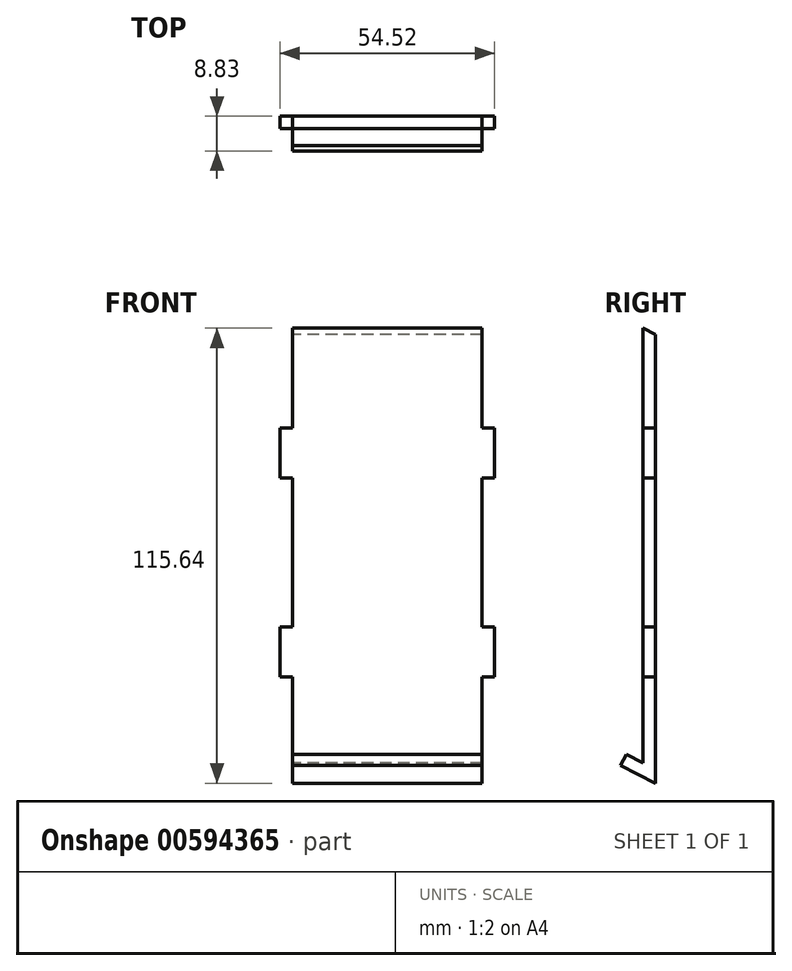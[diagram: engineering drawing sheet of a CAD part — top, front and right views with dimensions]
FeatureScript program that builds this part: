
annotation { "Feature Type Name" : "Feature", "Feature Type Description" : "" }
export const myFeature = defineFeature(function(context is Context, id is Id, definition is map)
    precondition{}
    {
        {
            var Q0;
            Q0=qCreatedBy(makeId("Front.planeOp"),FACE);
            var sketch = newSketch(context, id + "F0", { "sketchPlane" : qUnion([Q0])});
            skLineSegment(sketch, "E0.bottom", {"start": v(9.45, -57.01) * mm, "end": v(-34.96, -57.01) * mm});
            skLineSegment(sketch, "E0.top", {"start": v(13.2, 57.01) * mm, "end": v(-34.96, 57.01) * mm});
            skLineSegment(sketch, "E0.right", {"start": v(-38.14, -31.61) * mm, "end": v(-38.14, -18.91) * mm});
            skPoint(sketch, "E0.middle", {"position": v(0, 0) * mm});
            skLineSegment(sketch, "E1", {"start": v(-34.96, -57.01) * mm, "end": v(13.2, -57.01) * mm});
            skLineSegment(sketch, "E2", {"start": v(-34.96, 57.01) * mm, "end": v(-34.96, 31.61) * mm});
            skLineSegment(sketch, "E3", {"start": v(-34.96, 31.61) * mm, "end": v(-38.14, 31.61) * mm});
            skLineSegment(sketch, "E4", {"start": v(-38.14, 31.61) * mm, "end": v(-38.14, 18.91) * mm});
            skLineSegment(sketch, "E5", {"start": v(-38.14, 18.91) * mm, "end": v(-34.96, 18.91) * mm});
            skLineSegment(sketch, "E6", {"start": v(-34.96, 18.91) * mm, "end": v(-34.96, -18.91) * mm});
            skLineSegment(sketch, "E7", {"start": v(-34.96, -18.91) * mm, "end": v(-38.14, -18.91) * mm});
            skLineSegment(sketch, "E8", {"start": v(-38.14, -18.91) * mm, "end": v(-38.14, -31.61) * mm});
            skLineSegment(sketch, "E9", {"start": v(-38.14, -31.61) * mm, "end": v(-34.96, -31.61) * mm});
            skLineSegment(sketch, "E10", {"start": v(-34.96, -31.61) * mm, "end": v(-34.96, -57.01) * mm});
            skLineSegment(sketch, "E11.trimOffspring", {"start": v(-38.14, 18.91) * mm, "end": v(-38.14, 31.61) * mm});
            skPoint(sketch, "E12.end.orphan", {"position": v(9.45, -57.01) * mm});
            skLineSegment(sketch, "E13.MirrorCS", {"start": v(16.38, -31.61) * mm, "end": v(13.2, -31.61) * mm});
            skLineSegment(sketch, "E14.MirrorCS", {"start": v(16.38, 18.91) * mm, "end": v(13.2, 18.91) * mm});
            skLineSegment(sketch, "E15.MirrorCS", {"start": v(13.2, 31.61) * mm, "end": v(16.38, 31.61) * mm});
            skLineSegment(sketch, "E16.MirrorCS", {"start": v(13.2, -18.91) * mm, "end": v(16.38, -18.91) * mm});
            skLineSegment(sketch, "E17.MirrorCS", {"start": v(16.38, 31.61) * mm, "end": v(16.38, 18.91) * mm});
            skLineSegment(sketch, "E18.MirrorCS", {"start": v(16.38, -31.61) * mm, "end": v(16.38, -18.91) * mm});
            skLineSegment(sketch, "E19.MirrorCS", {"start": v(16.38, 18.91) * mm, "end": v(16.38, 31.61) * mm});
            skLineSegment(sketch, "E20.MirrorCS", {"start": v(13.2, 18.91) * mm, "end": v(13.2, -18.91) * mm});
            skLineSegment(sketch, "E21.MirrorCS", {"start": v(16.38, -18.91) * mm, "end": v(16.38, -31.61) * mm});
            skLineSegment(sketch, "E22", {"start": v(13.2, 31.61) * mm, "end": v(13.2, 57.01) * mm});
            skLineSegment(sketch, "E23", {"start": v(13.2, -31.61) * mm, "end": v(13.2, -57.01) * mm});
            skSolve(sketch);
        }
        {
            var Q0;
            Q0=qSketchRegion(id+"F0",true);
            extrude(context, id + "F1", {"entities" : qUnion([Q0]), "depth" : 3.17 * mm, "offsetDistance" : 25.4 * mm});
        }
        {
            var Q0;
            Q0=makeQuery(id+"F1.opExtrude","SWEPT_FACE",FACE,{"disambiguationData":[OSD([sQuery(id+"F0.wireOp",EDGE,"E10")])]});
            var sketch = newSketch(context, id + "F2", { "sketchPlane" : qUnion([Q0])});
            skLineSegment(sketch, "E24", {"start": v(3.17, -57.01) * mm, "end": v(8.83, -54.13) * mm});
            skLineSegment(sketch, "E25", {"start": v(8.83, -54.13) * mm, "end": v(7.4, -51.3) * mm});
            skLineSegment(sketch, "E26", {"start": v(7.4, -51.3) * mm, "end": v(0, -55.06) * mm});
            skLineSegment(sketch, "E27", {"start": v(0, -55.06) * mm, "end": v(0, -58.63) * mm});
            skLineSegment(sketch, "E28", {"start": v(3.17, -57.01) * mm, "end": v(0, -58.63) * mm});
            skSolve(sketch);
        }
        {
            var Q0;
            Q0=qSketchRegion(id+"F2",true);
            var Q1;
            {var subQ0=sQuery(id+"F2.wireOp",EDGE,"gtquZHyb-BIPY-AWKI-ODDM-ETVRPOuQAGwS");Q1=makeQuery(id+"F2.imprint","IMPRINT",FACE,{"disambiguationData":[TD([[makeQuery(id+"F2.imprint","IMPRINT",EDGE,{"derivedFrom":subQ0}),1.0]])]});}
            extrude(context, id + "F3", {"entities" : qUnion([Q0, Q1]), "operationType" : NewBodyOperationType.ADD, "oppositeDirection" : true, "depth" : 43.94 * mm, "offsetDistance" : 25.4 * mm});
        }
        {
            var Q0;
            Q0=makeQuery(id+"F1.opExtrude","SWEPT_FACE",FACE,{"disambiguationData":[OSD([sQuery(id+"F0.wireOp",EDGE,"E2")])]});
            var sketch = newSketch(context, id + "F4", { "sketchPlane" : qUnion([Q0])});
            skLineSegment(sketch, "E29", {"start": v(3.18, 57.01) * mm, "end": v(-2.5, 54.12) * mm});
            skLineSegment(sketch, "E30", {"start": v(3.18, 57.01) * mm, "end": v(0, 57.01) * mm});
            skLineSegment(sketch, "E31", {"start": v(0, 57.01) * mm, "end": v(0, 55.4) * mm});
            skSolve(sketch);
        }
        {
            var Q0;
            {var subQ0=sQuery(id+"F4.wireOp",EDGE,"E30");Q0=makeQuery(id+"F4.imprint","IMPRINT",FACE,{"disambiguationData":[TD([[makeQuery(id+"F4.imprint","IMPRINT",EDGE,{"derivedFrom":subQ0}),1.0]])]});}
            extrude(context, id + "F5", {"entities" : qUnion([Q0]), "operationType" : NewBodyOperationType.REMOVE, "oppositeDirection" : true, "depth" : 76.2 * mm, "offsetDistance" : 25.4 * mm});
        }
        {
            var Q0;
            Q0=qSketchRegion(id+"F2",true);
            extrude(context, id + "F6", {"entities" : qUnion([Q0]), "operationType" : NewBodyOperationType.ADD, "oppositeDirection" : true, "depth" : 48.17 * mm, "offsetDistance" : 25.4 * mm});
        }
    });
